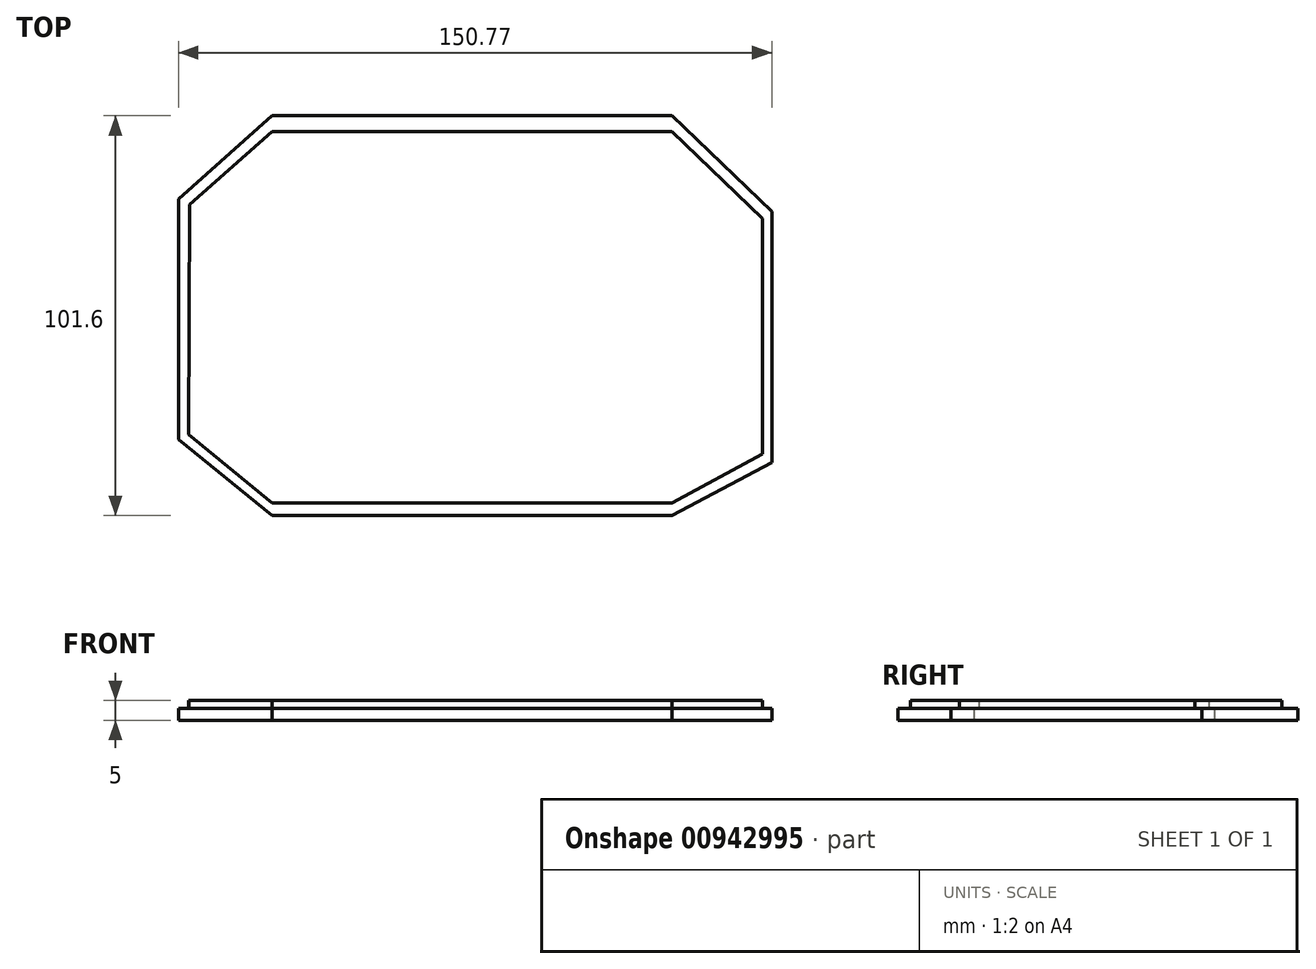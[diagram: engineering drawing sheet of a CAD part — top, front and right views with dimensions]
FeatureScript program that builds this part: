
annotation { "Feature Type Name" : "Feature", "Feature Type Description" : "" }
export const myFeature = defineFeature(function(context is Context, id is Id, definition is map)
    precondition{}
    {
        {
            var Q0;
            Q0=qCreatedBy(makeId("Top.planeOp"),FACE);
            var sketch = newSketch(context, id + "F0", { "sketchPlane" : qUnion([Q0])});
            skLineSegment(sketch, "E0.bottom", {"start": v(-50.8, 50.8) * mm, "end": v(50.8, 50.8) * mm});
            skLineSegment(sketch, "E0.top", {"start": v(-50.8, -50.8) * mm, "end": v(50.8, -50.8) * mm});
            skLineSegment(sketch, "E0.left", {"start": v(-50.8, 50.8) * mm, "end": v(-50.8, -50.8) * mm});
            skLineSegment(sketch, "E0.right", {"start": v(50.8, 50.8) * mm, "end": v(50.8, -50.8) * mm});
            skPoint(sketch, "E0.middle", {"position": v(0, 0) * mm});
            skLineSegment(sketch, "E1", {"start": v(-50.8, 50.8) * mm, "end": v(-74.55, 29.66) * mm});
            skLineSegment(sketch, "E2", {"start": v(-74.55, 29.66) * mm, "end": v(-74.55, -31.41) * mm});
            skLineSegment(sketch, "E3", {"start": v(-74.55, -31.41) * mm, "end": v(-50.8, -50.8) * mm});
            skLineSegment(sketch, "E4", {"start": v(50.8, 50.8) * mm, "end": v(76.22, 26.39) * mm});
            skLineSegment(sketch, "E5", {"start": v(76.22, 26.39) * mm, "end": v(76.22, -37.33) * mm});
            skLineSegment(sketch, "E6", {"start": v(76.22, -37.33) * mm, "end": v(50.8, -50.8) * mm});
            skLineSegment(sketch, "E7", {"start": v(-71.7, 28.26) * mm, "end": v(-50.8, 46.78) * mm});
            skLineSegment(sketch, "E8", {"start": v(-50.8, 46.78) * mm, "end": v(50.8, 46.78) * mm});
            skLineSegment(sketch, "E9", {"start": v(50.8, 46.78) * mm, "end": v(73.79, 24.69) * mm});
            skLineSegment(sketch, "E10", {"start": v(73.79, 24.69) * mm, "end": v(73.79, -35.13) * mm});
            skLineSegment(sketch, "E11", {"start": v(73.79, -35.13) * mm, "end": v(50.8, -47.54) * mm});
            skLineSegment(sketch, "E12", {"start": v(50.8, -47.54) * mm, "end": v(-50.8, -47.54) * mm});
            skLineSegment(sketch, "E13", {"start": v(-50.8, -47.54) * mm, "end": v(-72.03, -30.2) * mm});
            skLineSegment(sketch, "E14", {"start": v(-72.03, -30.2) * mm, "end": v(-71.7, 28.26) * mm});
            skSolve(sketch);
        }
        {
            var Q0;
            {var subQ0=sQuery(id+"F0.wireOp",EDGE,"E7");Q0=makeQuery(id+"F0.imprint","IMPRINT",FACE,{"disambiguationData":[TD([[makeQuery(id+"F0.imprint","IMPRINT",EDGE,{"derivedFrom":subQ0}),-1.0]])]});}
            var Q1;
            {var subQ0=sQuery(id+"F0.wireOp",EDGE,"E8");Q1=makeQuery(id+"F0.imprint","IMPRINT",FACE,{"disambiguationData":[TD([[makeQuery(id+"F0.imprint","IMPRINT",EDGE,{"derivedFrom":subQ0}),-1.0]])]});}
            var Q2;
            {var subQ0=sQuery(id+"F0.wireOp",EDGE,"E9");Q2=makeQuery(id+"F0.imprint","IMPRINT",FACE,{"disambiguationData":[TD([[makeQuery(id+"F0.imprint","IMPRINT",EDGE,{"derivedFrom":subQ0}),-1.0]])]});}
            extrude(context, id + "F1", {"entities" : qUnion([Q0, Q1, Q2]), "depth" : 5 * mm, "offsetDistance" : 25 * mm});
        }
        {
            var Q0;
            {var subQ0=sQuery(id+"F0.wireOp",EDGE,"E1");Q0=makeQuery(id+"F0.imprint","IMPRINT",FACE,{"disambiguationData":[TD([[makeQuery(id+"F0.imprint","IMPRINT",EDGE,{"derivedFrom":subQ0}),1.0]])]});}
            var Q1;
            {var subQ0=sQuery(id+"F0.wireOp",EDGE,"E0.bottom");Q1=makeQuery(id+"F0.imprint","IMPRINT",FACE,{"disambiguationData":[TD([[makeQuery(id+"F0.imprint","IMPRINT",EDGE,{"derivedFrom":subQ0}),-1.0]])]});}
            var Q2;
            {var subQ0=sQuery(id+"F0.wireOp",EDGE,"E4");Q2=makeQuery(id+"F0.imprint","IMPRINT",FACE,{"disambiguationData":[TD([[makeQuery(id+"F0.imprint","IMPRINT",EDGE,{"derivedFrom":subQ0}),-1.0]])]});}
            var Q3;
            {var subQ0=sQuery(id+"F0.wireOp",EDGE,"E0.top");Q3=makeQuery(id+"F0.imprint","IMPRINT",FACE,{"disambiguationData":[TD([[makeQuery(id+"F0.imprint","IMPRINT",EDGE,{"derivedFrom":subQ0}),1.0]])]});}
            extrude(context, id + "F2", {"entities" : qUnion([Q0, Q1, Q2, Q3]), "operationType" : NewBodyOperationType.ADD, "depth" : 3 * mm, "offsetDistance" : 25 * mm});
        }
    });
